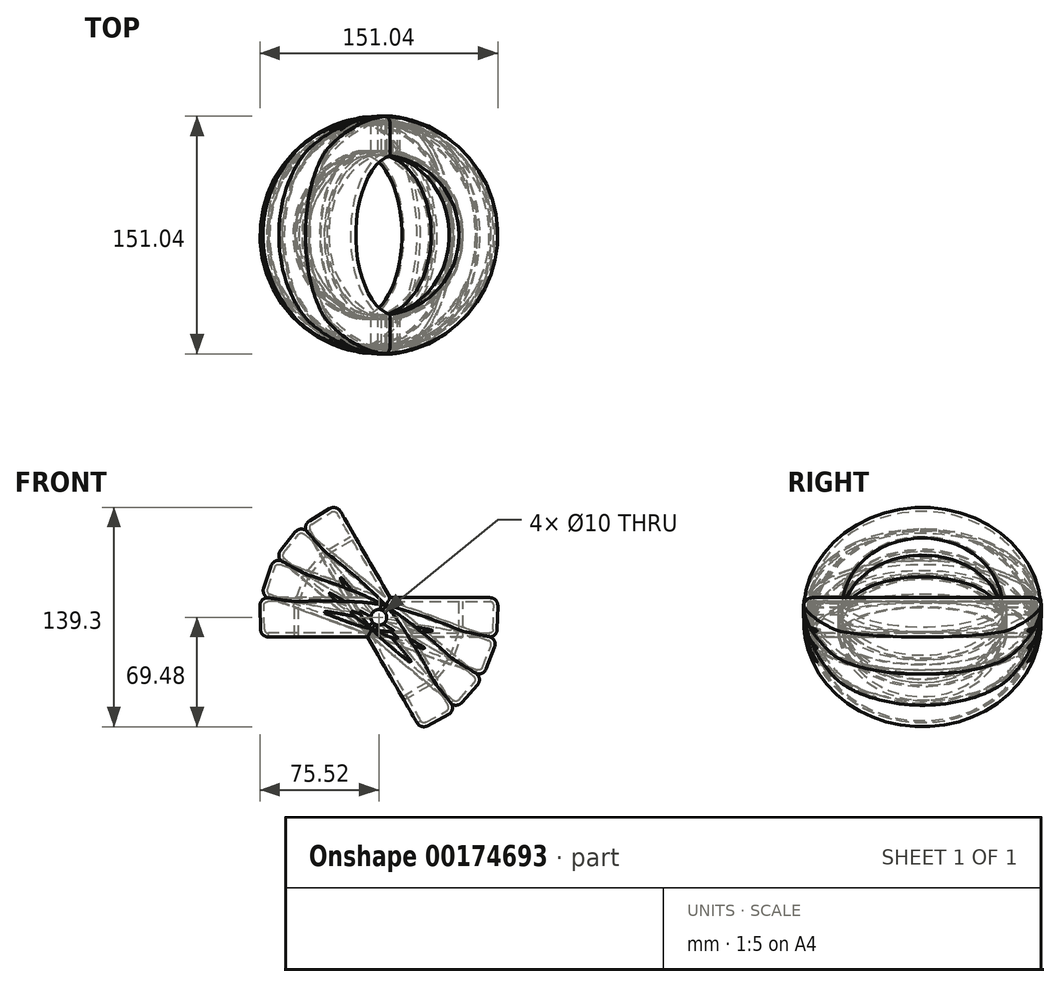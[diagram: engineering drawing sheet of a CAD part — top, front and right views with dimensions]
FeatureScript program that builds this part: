
annotation { "Feature Type Name" : "Feature", "Feature Type Description" : "" }
export const myFeature = defineFeature(function(context is Context, id is Id, definition is map)
    precondition{}
    {
        {
            var Q0;
            Q0=qCreatedBy(makeId("Top.planeOp"),FACE);
            var sketch = newSketch(context, id + "F0", { "sketchPlane" : qUnion([Q0])});
            skCircle(sketch, "E0", {"center": v(0, 0) * mm, "radius": 75 * mm});
            skSolve(sketch);
        }
        {
            var Q0;
            Q0 = qSketchRegion(id + "F0", true);
            extrude(context, id + "F1", {"entities" : qUnion([Q0]), "depth" : 25 * mm, "hasDraft" : true, "draftAngle" : 1.5 * degree});
        }
        {
            var Q0;
            Q0=makeQuery(id+"F1.opExtrude","CAP_FACE",FACE,{"disambiguationData":[OSD([sQuery(id+"F0.wireOp",EDGE,"E0")])],"isStart":false});
            var sketch = newSketch(context, id + "F2", { "sketchPlane" : qUnion([Q0])});
            skCircle(sketch, "E1", {"center": v(0, 0) * mm, "radius": 50.95 * mm});
            skSolve(sketch);
        }
        {
            var Q0;
            Q0=makeQuery(id+"F2.imprint","IMPRINT",FACE,{"disambiguationData":[TD([[makeQuery(id+"F2.imprint","IMPRINT",EDGE,{"derivedFrom":sQuery(id+"F2.wireOp",EDGE,"E1")}),1.0]])]});
            extrude(context, id + "F3", {"entities" : qUnion([Q0]), "operationType" : NewBodyOperationType.REMOVE, "oppositeDirection" : true, "depth" : 25 * mm});
        }
        {
            var Q0;
            Q0=makeQuery(id+"F1.opExtrude","CAP_EDGE",EDGE,{"disambiguationData":[OSD([sQuery(id+"F0.wireOp",EDGE,"E0")])],"isStart":true});
            var Q1;
            Q1=makeQuery(id+"F3.boolean.opBoolean","COPY",EDGE,{"derivedFrom":makeQuery(id+"F3.opExtrude","CAP_EDGE",EDGE,{"disambiguationData":[OSD([sQuery(id+"F2.wireOp",EDGE,"E1")])],"isStart":false})});
            var Q2;
            Q2=makeQuery(id+"F1.opExtrude","CAP_EDGE",EDGE,{"disambiguationData":[OSD([sQuery(id+"F0.wireOp",EDGE,"E0")])],"isStart":false});
            var Q3;
            Q3=makeQuery(id+"F3.boolean.opBoolean","COPY",EDGE,{"derivedFrom":makeQuery(id+"F3.opExtrude","CAP_EDGE",EDGE,{"disambiguationData":[OSD([sQuery(id+"F2.wireOp",EDGE,"E1")])],"isStart":true})});
            fillet(context, id + "F4", {"entities" : qUnion([Q0, Q1, Q2, Q3]), "radius" : 5 * mm, "tangentPropagation" : true, "allowEdgeOverflow" : false});
        }
        {
            var Q0;
            Q0=makeQuery(id+"F1.opExtrude","CAP_FACE",FACE,{"disambiguationData":[OSD([sQuery(id+"F0.wireOp",EDGE,"E0")])],"isStart":true});
            shell(context, id + "F5", {"entities" : qUnion([Q0]), "thickness" : 2.5 * mm});
        }
        {
            var Q0;
            Q0=qCreatedBy(makeId("Front.planeOp"),FACE);
            var sketch = newSketch(context, id + "F6", { "sketchPlane" : qUnion([Q0])});
            skLineSegment(sketch, "E2.0", {"start": v(-70.52, 25) * mm, "end": v(70.52, 25) * mm, "construction": true});
            skLineSegment(sketch, "E3.0", {"start": v(70.13, 0) * mm, "end": v(-70.13, 0) * mm, "construction": true});
            skLineSegment(sketch, "E4", {"start": v(0, 25) * mm, "end": v(0, 0) * mm, "construction": true});
            skCircle(sketch, "E5", {"center": v(0, 12.5) * mm, "radius": 5 * mm});
            skSolve(sketch);
        }
        {
            var Q0;
            Q0 = qSketchRegion(id + "F6", true);
            extrude(context, id + "F7", {"entities" : qUnion([Q0]), "operationType" : NewBodyOperationType.REMOVE, "endBound" : BoundingType.THROUGH_ALL, "oppositeDirection" : true, "depth" : 25 * mm, "hasSecondDirection" : true, "secondDirectionBound" : SecondDirectionBoundingType.THROUGH_ALL, "secondDirectionOppositeDirection" : false, "secondDirectionDepth" : 25 * mm});
        }
        {
            var Q0;
            Q0=makeQuery(id+"F1.opExtrude","SWEPT_BODY",BODY,{"disambiguationData":[OSD([sQuery(id+"F0.wireOp",EDGE,"E0")])]});
            var Q1;
            {var subQ0=sQuery(id+"F0.wireOp",EDGE,"E0");var subQ1=makeQuery(id+"F1.opExtrude","SWEPT_FACE",FACE,{"disambiguationData":[OSD([subQ0])]});Q1=makeQuery(id+"F7.boolean.opBoolean","COPY",FACE,{"disambiguationData":[TD([subQ1,makeQuery(id+"F5.opShell","OFFSET_FACE",FACE,{"disambiguationData":[OSD([subQ0]),TDD([subQ1])]})]),OD(1.0)],"derivedFrom":makeQuery(id+"F7.opExtrude","SWEPT_FACE",FACE,{"disambiguationData":[OSD([sQuery(id+"F6.wireOp",EDGE,"E5")])]})});}
            circularPattern(context, id + "F8", {"operationType" : NewBodyOperationType.ADD, "entities" : qUnion([Q0]), "axis" : qUnion([Q1]), "angle" : 60 * degree, "instanceCount" : 4, "equalSpace" : true});
        }
    });
